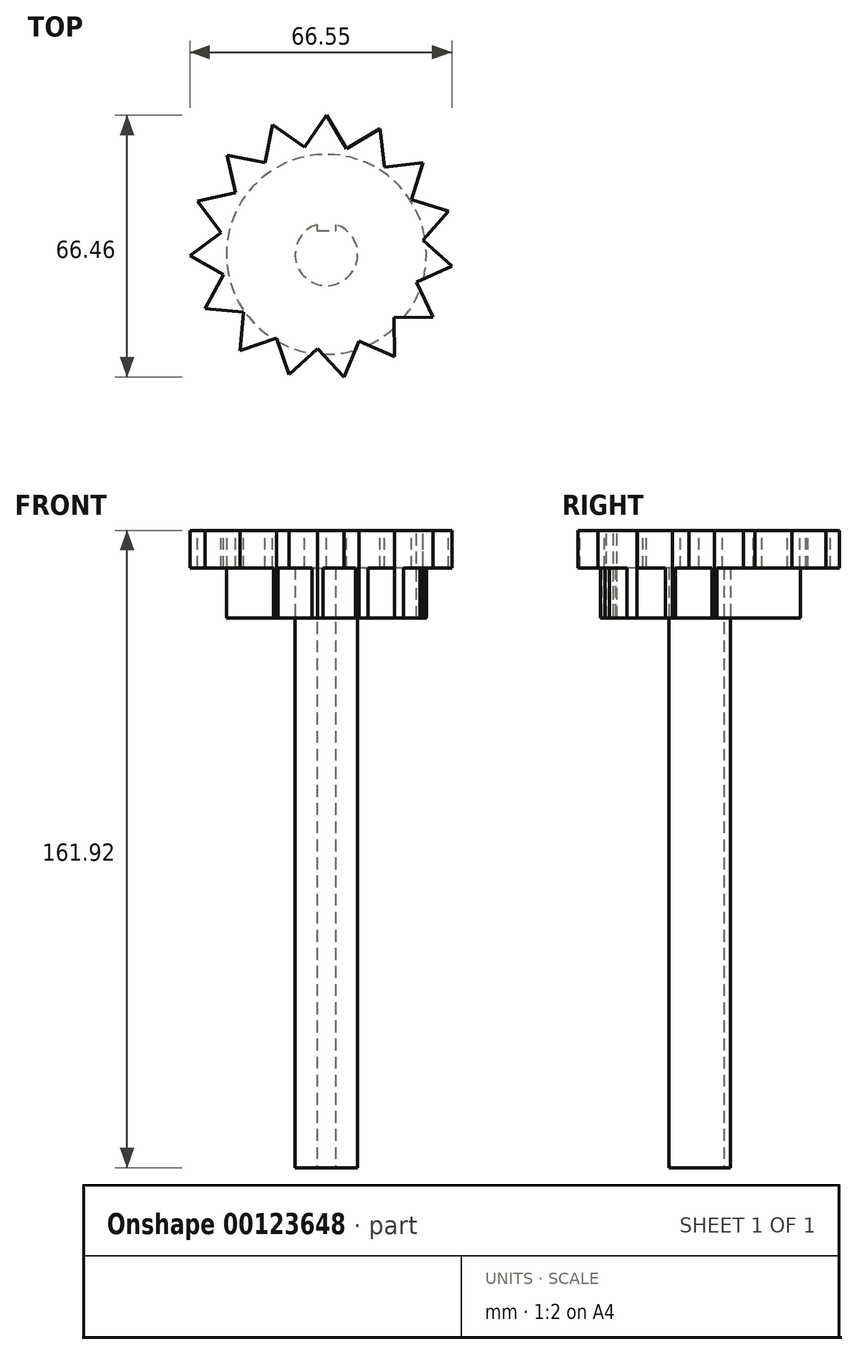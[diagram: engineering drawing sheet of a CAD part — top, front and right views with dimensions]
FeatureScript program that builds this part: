
annotation { "Feature Type Name" : "Feature", "Feature Type Description" : "" }
export const myFeature = defineFeature(function(context is Context, id is Id, definition is map)
    precondition{}
    {
        {
            var Q0;
            Q0=qCreatedBy(makeId("Top.planeOp"),FACE);
            var sketch = newSketch(context, id + "F0", { "sketchPlane" : qUnion([Q0])});
            skArc(sketch, "E0", {"start": v(-2.38, 7.57) * mm, "mid": v(0, -7.94) * mm, "end": v(2.38, 7.57) * mm});
            skLineSegment(sketch, "E1.top", {"start": v(-2.38, 5.98) * mm, "end": v(2.38, 5.98) * mm});
            skLineSegment(sketch, "E1.left", {"start": v(-2.38, 7.57) * mm, "end": v(-2.38, 5.98) * mm});
            skLineSegment(sketch, "E1.right", {"start": v(2.38, 7.57) * mm, "end": v(2.38, 5.98) * mm});
            skPoint(sketch, "E2", {"position": v(0, 5.98) * mm});
            skSolve(sketch);
        }
        {
            var Q0;
            Q0 = qSketchRegion(id + "F0", true);
            extrude(context, id + "F1", {"entities" : qUnion([Q0]), "endBound" : BoundingType.SYMMETRIC, "depth" : 152.4 * mm});
        }
        {
            var Q0;
            Q0=qCreatedBy(makeId("Top.planeOp"),FACE);
            var sketch = newSketch(context, id + "F2", { "sketchPlane" : qUnion([Q0])});
            skCircle(sketch, "E3", {"center": v(0, 0) * mm, "radius": 25.4 * mm});
            skArc(sketch, "E4.0", {"start": v(-2.38, 7.57) * mm, "mid": v(0, -7.94) * mm, "end": v(2.38, 7.57) * mm});
            skLineSegment(sketch, "E4.1", {"start": v(-2.38, 5.98) * mm, "end": v(2.38, 5.98) * mm});
            skLineSegment(sketch, "E4.2", {"start": v(-2.38, 7.57) * mm, "end": v(-2.38, 5.98) * mm});
            skLineSegment(sketch, "E4.3", {"start": v(2.38, 7.57) * mm, "end": v(2.38, 5.98) * mm});
            skSolve(sketch);
        }
        {
            var Q0;
            Q0 = qSketchRegion(id + "F2", true);
            var Q1;
            Q1=makeQuery(id+"F1.opExtrude","CAP_FACE",FACE,{"disambiguationData":[OSD([sQuery(id+"F0.wireOp",EDGE,"E0"),sQuery(id+"F0.wireOp",EDGE,"E1.top"),sQuery(id+"F0.wireOp",EDGE,"E1.left"),sQuery(id+"F0.wireOp",EDGE,"E1.right")])],"isStart":false});
            extrude(context, id + "F3", {"entities" : qUnion([Q0]), "endBound" : BoundingType.UP_TO_SURFACE, "endBoundEntityFace" : qUnion([Q1]), "depth" : 75.4 * mm, "hasSecondDirection" : true, "secondDirectionOppositeDirection" : false, "secondDirectionDepth" : 63.5 * mm, "hasSecondDirectionDraft" : true, "secondDirectionDraftAngle" : 10 * degree});
        }
        {
            var Q0;
            Q0=makeQuery(id+"F3.opExtrude","CAP_FACE",FACE,{"disambiguationData":[OSD([sQuery(id+"F2.wireOp",EDGE,"E3"),sQuery(id+"F2.wireOp",EDGE,"E4.0"),sQuery(id+"F2.wireOp",EDGE,"E4.1"),sQuery(id+"F2.wireOp",EDGE,"E4.2"),sQuery(id+"F2.wireOp",EDGE,"E4.3")])],"isStart":false});
            var sketch = newSketch(context, id + "F4", { "sketchPlane" : qUnion([Q0])});
            skCircle(sketch, "E5", {"center": v(0, 0) * mm, "radius": 35.69 * mm});
            skSolve(sketch);
        }
        {
            var Q0;
            Q0 = qSketchRegion(id + "F4", true);
            extrude(context, id + "F5", {"entities" : qUnion([Q0]), "depth" : 9.52 * mm});
        }
        {
            var Q0;
            Q0=makeQuery(id+"F3.opExtrude","SWEPT_BODY",BODY,{"disambiguationData":[OSD([sQuery(id+"F2.wireOp",EDGE,"E3"),sQuery(id+"F2.wireOp",EDGE,"E4.0"),sQuery(id+"F2.wireOp",EDGE,"E4.1"),sQuery(id+"F2.wireOp",EDGE,"E4.2"),sQuery(id+"F2.wireOp",EDGE,"E4.3")])]});
            var Q1;
            Q1=makeQuery(id+"F5.opExtrude","SWEPT_BODY",BODY,{"disambiguationData":[OSD([sQuery(id+"F4.wireOp",EDGE,"E5")])]});
            booleanBodies(context, id + "F6", {"operationType" : BooleanOperationType.UNION, "tools" : qUnion([Q0, Q1])});
        }
        {
            var Q0;
            Q0=makeQuery(id+"F5.opExtrude","CAP_FACE",FACE,{"disambiguationData":[OSD([sQuery(id+"F4.wireOp",EDGE,"E5")])],"isStart":false});
            var sketch = newSketch(context, id + "F7", { "sketchPlane" : qUnion([Q0])});
            skCircle(sketch, "E6.cCircle", {"center": v(0, 0) * mm, "radius": 35.69 * mm, "construction": true});
            skLineSegment(sketch, "E6.0", {"start": v(-13.66, -32.97) * mm, "end": v(-25.23, -25.23) * mm, "construction": true});
            skLineSegment(sketch, "E6.1", {"start": v(-25.23, -25.23) * mm, "end": v(-32.97, -13.66) * mm, "construction": true});
            skLineSegment(sketch, "E6.2", {"start": v(-32.97, -13.66) * mm, "end": v(-35.69, 0) * mm, "construction": true});
            skLineSegment(sketch, "E6.3", {"start": v(-35.69, 0) * mm, "end": v(-32.97, 13.66) * mm, "construction": true});
            skLineSegment(sketch, "E6.4", {"start": v(-32.97, 13.66) * mm, "end": v(-25.23, 25.23) * mm, "construction": true});
            skLineSegment(sketch, "E6.5", {"start": v(-25.23, 25.23) * mm, "end": v(-13.66, 32.97) * mm, "construction": true});
            skLineSegment(sketch, "E6.6", {"start": v(-13.66, 32.97) * mm, "end": v(0, 35.69) * mm, "construction": true});
            skLineSegment(sketch, "E6.7", {"start": v(0, 35.69) * mm, "end": v(13.66, 32.97) * mm, "construction": true});
            skLineSegment(sketch, "E6.8", {"start": v(13.66, 32.97) * mm, "end": v(25.23, 25.23) * mm, "construction": true});
            skLineSegment(sketch, "E6.9", {"start": v(25.23, 25.23) * mm, "end": v(32.97, 13.66) * mm, "construction": true});
            skLineSegment(sketch, "E6.10", {"start": v(32.97, 13.66) * mm, "end": v(35.69, 0) * mm, "construction": true});
            skLineSegment(sketch, "E6.11", {"start": v(35.69, 0) * mm, "end": v(32.97, -13.66) * mm, "construction": true});
            skLineSegment(sketch, "E6.12", {"start": v(32.97, -13.66) * mm, "end": v(25.23, -25.23) * mm, "construction": true});
            skLineSegment(sketch, "E6.13", {"start": v(25.23, -25.23) * mm, "end": v(13.66, -32.97) * mm, "construction": true});
            skLineSegment(sketch, "E6.14", {"start": v(13.66, -32.97) * mm, "end": v(0, -35.69) * mm, "construction": true});
            skLineSegment(sketch, "E6.15", {"start": v(0, -35.69) * mm, "end": v(-13.66, -32.97) * mm, "construction": true});
            skLineSegment(sketch, "E7", {"start": v(-25.23, 25.23) * mm, "end": v(-15.58, 23.31) * mm});
            skLineSegment(sketch, "E8", {"start": v(-15.58, 23.31) * mm, "end": v(-13.66, 32.97) * mm});
            skLineSegment(sketch, "E9.1.0", {"start": v(-13.66, 32.97) * mm, "end": v(-5.62, 27.29) * mm});
            skLineSegment(sketch, "E9.1.1", {"start": v(-5.62, 27.29) * mm, "end": v(0.07, 35.33) * mm});
            skLineSegment(sketch, "E9.2.0", {"start": v(0.07, 35.33) * mm, "end": v(5.1, 26.87) * mm});
            skLineSegment(sketch, "E9.2.1", {"start": v(5.1, 26.87) * mm, "end": v(13.56, 31.9) * mm});
            skLineSegment(sketch, "E9.3.0", {"start": v(13.56, 31.9) * mm, "end": v(14.72, 22.12) * mm});
            skLineSegment(sketch, "E9.3.1", {"start": v(14.72, 22.12) * mm, "end": v(24.5, 23.28) * mm});
            skLineSegment(sketch, "E9.4.0", {"start": v(24.5, 23.28) * mm, "end": v(21.58, 13.88) * mm});
            skLineSegment(sketch, "E9.4.1", {"start": v(21.58, 13.88) * mm, "end": v(30.98, 10.96) * mm});
            skLineSegment(sketch, "E9.5.0", {"start": v(30.98, 10.96) * mm, "end": v(24.49, 3.56) * mm});
            skLineSegment(sketch, "E9.5.1", {"start": v(24.49, 3.56) * mm, "end": v(31.9, -2.94) * mm});
            skLineSegment(sketch, "E9.6.0", {"start": v(31.9, -2.94) * mm, "end": v(22.95, -7.06) * mm});
            skLineSegment(sketch, "E9.6.1", {"start": v(22.95, -7.06) * mm, "end": v(27.07, -16) * mm});
            skLineSegment(sketch, "E9.7.0", {"start": v(27.07, -16) * mm, "end": v(17.23, -16.13) * mm});
            skLineSegment(sketch, "E9.7.1", {"start": v(17.23, -16.13) * mm, "end": v(17.36, -25.97) * mm});
            skLineSegment(sketch, "E9.8.0", {"start": v(17.36, -25.97) * mm, "end": v(8.3, -22.09) * mm});
            skLineSegment(sketch, "E9.8.1", {"start": v(8.3, -22.09) * mm, "end": v(4.42, -31.13) * mm});
            skLineSegment(sketch, "E9.9.0", {"start": v(4.42, -31.13) * mm, "end": v(-2.26, -23.9) * mm});
            skLineSegment(sketch, "E9.9.1", {"start": v(-2.26, -23.9) * mm, "end": v(-9.5, -30.59) * mm});
            skLineSegment(sketch, "E9.10.0", {"start": v(-9.5, -30.59) * mm, "end": v(-12.66, -21.26) * mm});
            skLineSegment(sketch, "E9.10.1", {"start": v(-12.66, -21.26) * mm, "end": v(-21.98, -24.43) * mm});
            skLineSegment(sketch, "E9.11.0", {"start": v(-21.98, -24.43) * mm, "end": v(-21.08, -14.62) * mm});
            skLineSegment(sketch, "E9.11.1", {"start": v(-21.08, -14.62) * mm, "end": v(-30.88, -13.72) * mm});
            skLineSegment(sketch, "E9.12.0", {"start": v(-30.88, -13.72) * mm, "end": v(-26.07, -5.13) * mm});
            skLineSegment(sketch, "E9.12.1", {"start": v(-26.07, -5.13) * mm, "end": v(-34.66, -0.32) * mm});
            skLineSegment(sketch, "E9.13.0", {"start": v(-34.66, -0.32) * mm, "end": v(-26.77, 5.57) * mm});
            skLineSegment(sketch, "E9.13.1", {"start": v(-26.77, 5.57) * mm, "end": v(-32.66, 13.46) * mm});
            skLineSegment(sketch, "E9.14.0", {"start": v(-32.66, 13.46) * mm, "end": v(-23.06, 15.63) * mm});
            skLineSegment(sketch, "E9.14.1", {"start": v(-23.06, 15.63) * mm, "end": v(-25.23, 25.23) * mm});
            skPoint(sketch, "E9.center", {"position": v(-1.25, 1.87) * mm});
            skLineSegment(sketch, "E9.anchor1", {"start": v(-1.25, 1.87) * mm, "end": v(-25.23, 25.23) * mm, "construction": true});
            skLineSegment(sketch, "E9.anchor2", {"start": v(-1.25, 1.87) * mm, "end": v(-25.77, 27.8) * mm, "construction": true});
            skSolve(sketch);
        }
        {
            var Q0;
            Q0 = qSketchRegion(id + "F7", true);
            var Q1;
            {var subQ0=sQuery(id+"F4.wireOp",EDGE,"E5");Q1=makeQuery(id+"F6.opBoolean","SPLIT",FACE,{"disambiguationData":[TD([makeQuery(id+"F3.opExtrude","SWEPT_FACE",FACE,{"disambiguationData":[OSD([sQuery(id+"F2.wireOp",EDGE,"E3")])]})])],"derivedFrom":makeQuery(id+"F5.opExtrude","CAP_FACE",FACE,{"disambiguationData":[OSD([subQ0])],"isStart":true})});}
            extrude(context, id + "F8", {"entities" : qUnion([Q0]), "operationType" : NewBodyOperationType.INTERSECT, "endBound" : BoundingType.THROUGH_ALL, "oppositeDirection" : true, "endBoundEntityFace" : qUnion([Q1]), "depth" : 25.4 * mm});
        }
    });
